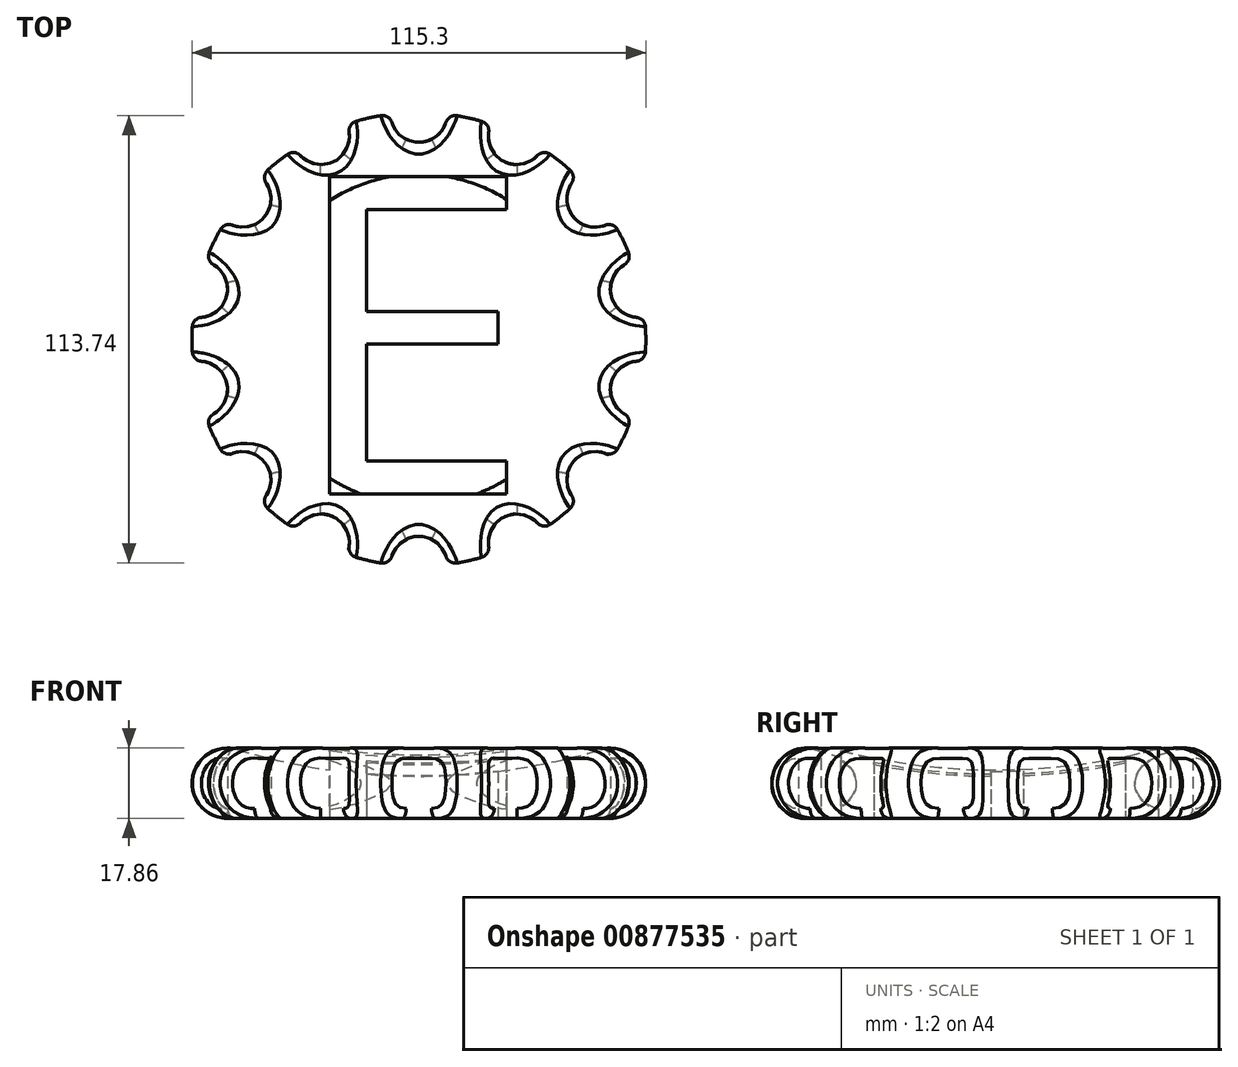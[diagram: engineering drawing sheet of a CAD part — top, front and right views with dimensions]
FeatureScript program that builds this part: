
annotation { "Feature Type Name" : "Feature", "Feature Type Description" : "" }
export const myFeature = defineFeature(function(context is Context, id is Id, definition is map)
    precondition{}
    {
        {
            var Q0;
            Q0=qCreatedBy(makeId("Front.planeOp"),FACE);
            var sketch = newSketch(context, id + "F0", { "sketchPlane" : qUnion([Q0])});
            skArc(sketch, "E0", {"start": v(-46.16, 17.48) * mm, "mid": v(-57.56, 10.22) * mm, "end": v(-48.72, 0) * mm});
            skArc(sketch, "E1", {"start": v(-46.16, 17.48) * mm, "mid": v(-23.33, 12.41) * mm, "end": v(0, 10.71) * mm});
            skLineSegment(sketch, "E2", {"start": v(0, 0) * mm, "end": v(0, 10.71) * mm});
            skLineSegment(sketch, "E3", {"start": v(0, 10.71) * mm, "end": v(0, 0) * mm});
            skLineSegment(sketch, "E4", {"start": v(0, 0) * mm, "end": v(-48.72, 0) * mm});
            skSolve(sketch);
        }
        {
            var Q0;
            Q0=makeQuery(id+"F0.imprint","IMPRINT",FACE,{"disambiguationData":[TD([[makeQuery(id+"F0.imprint","IMPRINT",EDGE,{"derivedFrom":sQuery(id+"F0.wireOp",EDGE,"E0")}),1.0]])]});
            var Q1;
            Q1=sQuery(id+"F0.wireOp",EDGE,"E2");
            revolve(context, id + "F1", {"surfaceOperationType" : NewSurfaceOperationType.NEW, "entities" : qUnion([Q0]), "axis" : qUnion([Q1]), "revolveType" : RevolveType.FULL});
        }
        {
            var Q0;
            Q0=qCreatedBy(makeId("Top.planeOp"),FACE);
            var sketch = newSketch(context, id + "F2", { "sketchPlane" : qUnion([Q0])});
            skText(sketch, "E5", { "text": "E", "fontName": "OpenSans-Regular.ttf"});
            const initialGuessF2  = {"E5": [-0.03371, -0.03926, 1, 0, 0.08128]};
            skSetInitialGuess(sketch, initialGuessF2);
            skSolve(sketch);
        }
        {
            var Q0;
            Q0 = qSketchRegion(id + "F2", true);
            var Q1;
            Q1 = qSketchRegion(id + "F4", true);
            extrude(context, id + "F3", {"entities" : qUnion([Q0, Q1]), "operationType" : NewBodyOperationType.REMOVE, "depth" : 25.4 * mm, "offsetDistance" : 25.4 * mm});
        }
        {
            var Q0;
            Q0=qCreatedBy(makeId("Top.planeOp"),FACE);
            var sketch = newSketch(context, id + "F4", { "sketchPlane" : qUnion([Q0])});
            skCircle(sketch, "E6", {"center": v(0, 57.23) * mm, "radius": 7.17 * mm});
            skCircle(sketch, "E7.1.0", {"center": v(-24.83, 51.56) * mm, "radius": 7.17 * mm});
            skCircle(sketch, "E7.2.0", {"center": v(-44.74, 35.68) * mm, "radius": 7.17 * mm});
            skCircle(sketch, "E7.3.0", {"center": v(-55.8, 12.73) * mm, "radius": 7.17 * mm});
            skCircle(sketch, "E7.4.0", {"center": v(-55.8, -12.73) * mm, "radius": 7.17 * mm});
            skCircle(sketch, "E7.5.0", {"center": v(-44.74, -35.68) * mm, "radius": 7.17 * mm});
            skCircle(sketch, "E7.6.0", {"center": v(-24.83, -51.56) * mm, "radius": 7.17 * mm});
            skCircle(sketch, "E7.7.0", {"center": v(0, -57.23) * mm, "radius": 7.17 * mm});
            skCircle(sketch, "E7.8.0", {"center": v(24.83, -51.56) * mm, "radius": 7.17 * mm});
            skCircle(sketch, "E7.9.0", {"center": v(44.74, -35.68) * mm, "radius": 7.17 * mm});
            skPoint(sketch, "E7.center", {"position": v(0, 0) * mm});
            skCircle(sketch, "E8.1.10.0", {"center": v(55.8, -12.73) * mm, "radius": 7.17 * mm});
            skCircle(sketch, "E9.1.11.0", {"center": v(55.8, 12.73) * mm, "radius": 7.17 * mm});
            skCircle(sketch, "E9.1.12.0", {"center": v(44.74, 35.68) * mm, "radius": 7.17 * mm});
            skCircle(sketch, "E9.1.13.0", {"center": v(24.83, 51.56) * mm, "radius": 7.17 * mm});
            skSolve(sketch);
        }
        {
            var Q0;
            Q0=qCreatedBy(makeId("Front.planeOp"),FACE);
            var sketch = newSketch(context, id + "F5", { "sketchPlane" : qUnion([Q0])});
            skCircle(sketch, "E10", {"center": v(-48.72, 8.93) * mm, "radius": 6.79 * mm});
            skSolve(sketch);
        }
        {
            var Q0;
            Q0 = qSketchRegion(id + "F5", true);
            var Q1;
            Q1=sQuery(id+"F0.wireOp",EDGE,"E2");
            revolve(context, id + "F6", {"operationType" : NewBodyOperationType.ADD, "surfaceOperationType" : NewSurfaceOperationType.NEW, "entities" : qUnion([Q0]), "axis" : qUnion([Q1]), "revolveType" : RevolveType.FULL});
        }
        {
            var Q0;
            Q0 = qSketchRegion(id + "F4", true);
            extrude(context, id + "F7", {"entities" : qUnion([Q0]), "operationType" : NewBodyOperationType.REMOVE, "depth" : 25.4 * mm, "offsetDistance" : 25.4 * mm});
        }
        {
            var Q0;
            Q0=makeQuery(id+"F7.boolean.opBoolean","INTERSECT",EDGE,{"derivedFrom":[makeQuery(id+"F1.opRevolve","SWEPT_FACE",FACE,{"disambiguationData":[OSD([sQuery(id+"F0.wireOp",EDGE,"E0")])]}),makeQuery(id+"F7.opExtrude","SWEPT_FACE",FACE,{"disambiguationData":[OSD([sQuery(id+"F4.wireOp",EDGE,"E9.1.12.0")])]})]});
            var Q1;
            Q1=makeQuery(id+"F7.boolean.opBoolean","INTERSECT",EDGE,{"derivedFrom":[makeQuery(id+"F1.opRevolve","SWEPT_FACE",FACE,{"disambiguationData":[OSD([sQuery(id+"F0.wireOp",EDGE,"E0")])]}),makeQuery(id+"F7.opExtrude","SWEPT_FACE",FACE,{"disambiguationData":[OSD([sQuery(id+"F4.wireOp",EDGE,"E9.1.13.0")])]})]});
            var Q2;
            Q2=makeQuery(id+"F7.boolean.opBoolean","INTERSECT",EDGE,{"derivedFrom":[makeQuery(id+"F1.opRevolve","SWEPT_FACE",FACE,{"disambiguationData":[OSD([sQuery(id+"F0.wireOp",EDGE,"E0")])]}),makeQuery(id+"F7.opExtrude","SWEPT_FACE",FACE,{"disambiguationData":[OSD([sQuery(id+"F4.wireOp",EDGE,"E6")])]})]});
            var Q3;
            Q3=makeQuery(id+"F7.boolean.opBoolean","INTERSECT",EDGE,{"derivedFrom":[makeQuery(id+"F1.opRevolve","SWEPT_FACE",FACE,{"disambiguationData":[OSD([sQuery(id+"F0.wireOp",EDGE,"E0")])]}),makeQuery(id+"F7.opExtrude","SWEPT_FACE",FACE,{"disambiguationData":[OSD([sQuery(id+"F4.wireOp",EDGE,"E7.4.0")])]})]});
            var Q4;
            Q4=makeQuery(id+"F7.boolean.opBoolean","INTERSECT",EDGE,{"derivedFrom":[makeQuery(id+"F1.opRevolve","SWEPT_FACE",FACE,{"disambiguationData":[OSD([sQuery(id+"F0.wireOp",EDGE,"E0")])]}),makeQuery(id+"F7.opExtrude","SWEPT_FACE",FACE,{"disambiguationData":[OSD([sQuery(id+"F4.wireOp",EDGE,"E7.5.0")])]})]});
            var Q5;
            Q5=makeQuery(id+"F7.boolean.opBoolean","INTERSECT",EDGE,{"derivedFrom":[makeQuery(id+"F1.opRevolve","SWEPT_FACE",FACE,{"disambiguationData":[OSD([sQuery(id+"F0.wireOp",EDGE,"E0")])]}),makeQuery(id+"F7.opExtrude","SWEPT_FACE",FACE,{"disambiguationData":[OSD([sQuery(id+"F4.wireOp",EDGE,"E7.5.0")])]})]});
            var Q6;
            Q6=makeQuery(id+"F7.boolean.opBoolean","INTERSECT",EDGE,{"derivedFrom":[makeQuery(id+"F1.opRevolve","SWEPT_FACE",FACE,{"disambiguationData":[OSD([sQuery(id+"F0.wireOp",EDGE,"E0")])]}),makeQuery(id+"F7.opExtrude","SWEPT_FACE",FACE,{"disambiguationData":[OSD([sQuery(id+"F4.wireOp",EDGE,"E7.6.0")])]})]});
            var Q7;
            Q7=makeQuery(id+"F7.boolean.opBoolean","INTERSECT",EDGE,{"derivedFrom":[makeQuery(id+"F1.opRevolve","SWEPT_FACE",FACE,{"disambiguationData":[OSD([sQuery(id+"F0.wireOp",EDGE,"E0")])]}),makeQuery(id+"F7.opExtrude","SWEPT_FACE",FACE,{"disambiguationData":[OSD([sQuery(id+"F4.wireOp",EDGE,"E7.7.0")])]})]});
            var Q8;
            Q8=makeQuery(id+"F7.boolean.opBoolean","INTERSECT",EDGE,{"derivedFrom":[makeQuery(id+"F1.opRevolve","SWEPT_FACE",FACE,{"disambiguationData":[OSD([sQuery(id+"F0.wireOp",EDGE,"E0")])]}),makeQuery(id+"F7.opExtrude","SWEPT_FACE",FACE,{"disambiguationData":[OSD([sQuery(id+"F4.wireOp",EDGE,"E7.8.0")])]})]});
            var Q9;
            Q9=makeQuery(id+"F7.boolean.opBoolean","INTERSECT",EDGE,{"derivedFrom":[makeQuery(id+"F1.opRevolve","SWEPT_FACE",FACE,{"disambiguationData":[OSD([sQuery(id+"F0.wireOp",EDGE,"E0")])]}),makeQuery(id+"F7.opExtrude","SWEPT_FACE",FACE,{"disambiguationData":[OSD([sQuery(id+"F4.wireOp",EDGE,"E7.6.0")])]})]});
            var Q10;
            Q10=makeQuery(id+"F7.boolean.opBoolean","INTERSECT",EDGE,{"derivedFrom":[makeQuery(id+"F1.opRevolve","SWEPT_FACE",FACE,{"disambiguationData":[OSD([sQuery(id+"F0.wireOp",EDGE,"E0")])]}),makeQuery(id+"F7.opExtrude","SWEPT_FACE",FACE,{"disambiguationData":[OSD([sQuery(id+"F4.wireOp",EDGE,"E7.7.0")])]})]});
            var Q11;
            Q11=makeQuery(id+"F7.boolean.opBoolean","INTERSECT",EDGE,{"derivedFrom":[makeQuery(id+"F1.opRevolve","SWEPT_FACE",FACE,{"disambiguationData":[OSD([sQuery(id+"F0.wireOp",EDGE,"E0")])]}),makeQuery(id+"F7.opExtrude","SWEPT_FACE",FACE,{"disambiguationData":[OSD([sQuery(id+"F4.wireOp",EDGE,"E7.8.0")])]})]});
            var Q12;
            Q12=makeQuery(id+"F7.boolean.opBoolean","INTERSECT",EDGE,{"derivedFrom":[makeQuery(id+"F1.opRevolve","SWEPT_FACE",FACE,{"disambiguationData":[OSD([sQuery(id+"F0.wireOp",EDGE,"E0")])]}),makeQuery(id+"F7.opExtrude","SWEPT_FACE",FACE,{"disambiguationData":[OSD([sQuery(id+"F4.wireOp",EDGE,"E7.9.0")])]})]});
            var Q13;
            Q13=makeQuery(id+"F7.boolean.opBoolean","INTERSECT",EDGE,{"derivedFrom":[makeQuery(id+"F1.opRevolve","SWEPT_FACE",FACE,{"disambiguationData":[OSD([sQuery(id+"F0.wireOp",EDGE,"E0")])]}),makeQuery(id+"F7.opExtrude","SWEPT_FACE",FACE,{"disambiguationData":[OSD([sQuery(id+"F4.wireOp",EDGE,"E8.1.10.0")])]})]});
            var Q14;
            Q14=makeQuery(id+"F7.boolean.opBoolean","INTERSECT",EDGE,{"derivedFrom":[makeQuery(id+"F1.opRevolve","SWEPT_FACE",FACE,{"disambiguationData":[OSD([sQuery(id+"F0.wireOp",EDGE,"E0")])]}),makeQuery(id+"F7.opExtrude","SWEPT_FACE",FACE,{"disambiguationData":[OSD([sQuery(id+"F4.wireOp",EDGE,"E9.1.11.0")])]})]});
            var Q15;
            Q15=makeQuery(id+"F7.boolean.opBoolean","INTERSECT",EDGE,{"derivedFrom":[makeQuery(id+"F1.opRevolve","SWEPT_FACE",FACE,{"disambiguationData":[OSD([sQuery(id+"F0.wireOp",EDGE,"E0")])]}),makeQuery(id+"F7.opExtrude","SWEPT_FACE",FACE,{"disambiguationData":[OSD([sQuery(id+"F4.wireOp",EDGE,"E7.7.0")])]})]});
            var Q16;
            Q16=makeQuery(id+"F7.boolean.opBoolean","INTERSECT",EDGE,{"derivedFrom":[makeQuery(id+"F1.opRevolve","SWEPT_FACE",FACE,{"disambiguationData":[OSD([sQuery(id+"F0.wireOp",EDGE,"E0")])]}),makeQuery(id+"F7.opExtrude","SWEPT_FACE",FACE,{"disambiguationData":[OSD([sQuery(id+"F4.wireOp",EDGE,"E7.8.0")])]})]});
            var Q17;
            Q17=makeQuery(id+"F7.boolean.opBoolean","INTERSECT",EDGE,{"derivedFrom":[makeQuery(id+"F1.opRevolve","SWEPT_FACE",FACE,{"disambiguationData":[OSD([sQuery(id+"F0.wireOp",EDGE,"E0")])]}),makeQuery(id+"F7.opExtrude","SWEPT_FACE",FACE,{"disambiguationData":[OSD([sQuery(id+"F4.wireOp",EDGE,"E7.9.0")])]})]});
            var Q18;
            Q18=makeQuery(id+"F7.boolean.opBoolean","INTERSECT",EDGE,{"derivedFrom":[makeQuery(id+"F1.opRevolve","SWEPT_FACE",FACE,{"disambiguationData":[OSD([sQuery(id+"F0.wireOp",EDGE,"E0")])]}),makeQuery(id+"F7.opExtrude","SWEPT_FACE",FACE,{"disambiguationData":[OSD([sQuery(id+"F4.wireOp",EDGE,"E7.8.0")])]})]});
            var Q19;
            Q19=makeQuery(id+"F7.boolean.opBoolean","INTERSECT",EDGE,{"derivedFrom":[makeQuery(id+"F1.opRevolve","SWEPT_FACE",FACE,{"disambiguationData":[OSD([sQuery(id+"F0.wireOp",EDGE,"E0")])]}),makeQuery(id+"F7.opExtrude","SWEPT_FACE",FACE,{"disambiguationData":[OSD([sQuery(id+"F4.wireOp",EDGE,"E7.8.0")])]})]});
            var Q20;
            Q20=makeQuery(id+"F7.boolean.opBoolean","INTERSECT",EDGE,{"derivedFrom":[makeQuery(id+"F1.opRevolve","SWEPT_FACE",FACE,{"disambiguationData":[OSD([sQuery(id+"F0.wireOp",EDGE,"E0")])]}),makeQuery(id+"F7.opExtrude","SWEPT_FACE",FACE,{"disambiguationData":[OSD([sQuery(id+"F4.wireOp",EDGE,"E7.8.0")])]})]});
            fillet(context, id + "F8", {"entities" : qUnion([Q0, Q1, Q2, Q3, Q4, Q5, Q6, Q7, Q8, Q9, Q10, Q11, Q12, Q13, Q14, Q15, Q16, Q17, Q18, Q19, Q20]), "radius" : 2.54 * mm, "tangentPropagation" : true, "allowEdgeOverflow" : false});
        }
        {
            var Q0;
            Q0=makeQuery(id+"F7.boolean.opBoolean","INTERSECT",EDGE,{"derivedFrom":[makeQuery(id+"F1.opRevolve","SWEPT_FACE",FACE,{"disambiguationData":[OSD([sQuery(id+"F0.wireOp",EDGE,"E0")])]}),makeQuery(id+"F7.opExtrude","SWEPT_FACE",FACE,{"disambiguationData":[OSD([sQuery(id+"F4.wireOp",EDGE,"E7.1.0")])]})]});
            var Q1;
            Q1=makeQuery(id+"F7.boolean.opBoolean","INTERSECT",EDGE,{"derivedFrom":[makeQuery(id+"F1.opRevolve","SWEPT_FACE",FACE,{"disambiguationData":[OSD([sQuery(id+"F0.wireOp",EDGE,"E0")])]}),makeQuery(id+"F7.opExtrude","SWEPT_FACE",FACE,{"disambiguationData":[OSD([sQuery(id+"F4.wireOp",EDGE,"E7.2.0")])]})]});
            var Q2;
            Q2=makeQuery(id+"F7.boolean.opBoolean","INTERSECT",EDGE,{"derivedFrom":[makeQuery(id+"F1.opRevolve","SWEPT_FACE",FACE,{"disambiguationData":[OSD([sQuery(id+"F0.wireOp",EDGE,"E0")])]}),makeQuery(id+"F7.opExtrude","SWEPT_FACE",FACE,{"disambiguationData":[OSD([sQuery(id+"F4.wireOp",EDGE,"E7.3.0")])]})]});
            fillet(context, id + "F9", {"entities" : qUnion([Q0, Q1, Q2]), "radius" : 2.54 * mm, "tangentPropagation" : true, "allowEdgeOverflow" : false});
        }
    });
